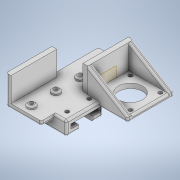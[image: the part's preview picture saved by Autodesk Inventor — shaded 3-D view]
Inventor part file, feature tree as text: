
AUTODESK INVENTOR PART (.ipt)
format: ipt  version: 2020.4 (Build 244396000, 396)  size: 435,200 bytes
history: native  units: in
note: dims shown in document units (in); Inventor stores cm internally (conversion verified against a paired STEP export)
features: sketch x20, extrude x19, chamfer x3, fillet x2, plane x1
ambient origin geometry x8: Origin, YZ Plane, XZ Plane, XY Plane, X Axis, Y Axis, Z Axis, Center Point
bodies: Solid1 (feature_tree)
feature tree (45):
  extrude  "Extrusion1"  Depth=2.6378in
  extrude  "Extrusion8"  Depth=0.3406in
  chamfer  "Chamfer1"  Distance=0.1181in
  extrude  "Extrusion9"  Depth=0.0787in
  extrude  "Extrusion10"  Depth=0.1575in
  extrude  "Extrusion11"  Depth=0.2362in
  extrude  "Extrusion12"  Depth=0.2362in
  extrude  "Extrusion13"  Depth=1.6142in
  extrude  "Extrusion14"  Depth=0.5709in
  extrude  "Extrusion15"  Depth=0.4724in
  extrude  "Extrusion16"  Depth=0.4724in
  chamfer  "Chamfer2"  Distance=1.4331in
  plane  "Work Plane1"
  extrude  "Extrusion17"  Depth=0.1575in
  extrude  "Extrusion18"  Depth=0.0394in
  extrude  "Extrusion19"  Depth=0.5118in TaperAngle=0.0deg
  chamfer  "Chamfer3"  Distance=1.0236in
  extrude  "Extrusion20"  Depth=0.0197in
  extrude  "Extrusion21"  Depth=0.0197in TaperAngle=0.0deg
  sketch  "Sketch22"  dims[d68=0.1181in d69=1.4331in d70=0.0in]
  extrude  "Extrusion22"  Depth=0.0787in TaperAngle=45.0deg
  extrude  "Extrusion23"  Depth=0.0197in
  extrude  "Extrusion24"  Depth=0.0197in
  extrude  "Extrusion25"  Depth=0.0197in TaperAngle=0.0deg
  fillet  "Fillet5"  Radius=0.2362in
  fillet  "Fillet6"  Radius=0.0984in
  sketch  "Sketch1"  dims[d0=1.4331in d1=2.6378in]
  sketch  "Sketch8"  dims[d2=0.1969in d3=0.0in d37=0.3406in]
  sketch  "Sketch9"  dims[d38=0.3406in]
  sketch  "Sketch10"  dims[d39=0.3406in d40=0.1181in d41=0.0in]
  sketch  "Sketch11"  dims[d42=0.0591in d43=0.0787in d44=45.0deg d45=0.1575in]
  sketch  "Sketch12"  dims[d46=0.1575in d47=0.1575in]
  sketch  "Sketch13"  dims[d48=0.7874in d49=0.0in d50=0.2362in]
  sketch  "Sketch14"  dims[d51=0.2362in d52=0.2362in]
  sketch  "Sketch15"  dims[d53=0.0984in d54=0.0in d55=1.6142in]
  sketch  "Sketch16"  dims[d56=0.1969in d57=0.5709in]
  sketch  "Sketch17"  dims[d58=0.1969in d59=0.4724in]
  sketch  "Sketch18"  dims[d60=0.1969in d61=0.4724in]
  sketch  "Sketch19"  dims[d62=0.1969in]
  sketch  "Sketch20"  dims[d63=0.5118in d64=1.4331in d65=0.0in d66=0.0in]
  sketch  "Sketch21"  dims[d67=0.1181in]
  sketch  "Sketch23"  dims[d71=0.1575in d72=0.1575in]
  sketch  "Sketch24"  dims[d73=1.4331in d74=0.0in d75=0.0394in]
  sketch  "Sketch25"  dims[d76=0.0394in d77=0.5118in d78=0.0in d80=1.0236in d81=0.0in]
  sketch  "Sketch26"  dims[d82=0.5118in d83=0.1181in d84=0.374in d85=0.0in d86=0.1181in d87=0.0787in d88=45.0deg d89=1.6535in d90=0.1969in d91=1.6535in d92=0.0in d94=0.2362in d95=0.0984in d96=0.0in d97=0.3406in d98=0.1181in d99=0.0in d100=0.0591in d101=0.0787in d102=45.0deg d103=0.1575in d104=0.3937in d105=0.0in d106=0.9843in d107=0.1575in d108=0.1575in d109=0.1575in d110=0.1575in d111=0.3937in d112=0.0in d113=0.1181in d114=0.0in d115=0.1181in d116=0.0in d117=0.1969in d118=1.8701in d119=0.1969in d120=1.8701in d121=0.1969in d122=0.1969in d123=1.0in d124=0.0in d125=1.9685in d126=0.0in d127=0.0787in d128=0.0787in d8=0.0197in d9=0.0344in d10=0.0197in d11=0.0344in d13=0.0197in d14=0.0344in d15=0.0197in d16=0.0344in]
